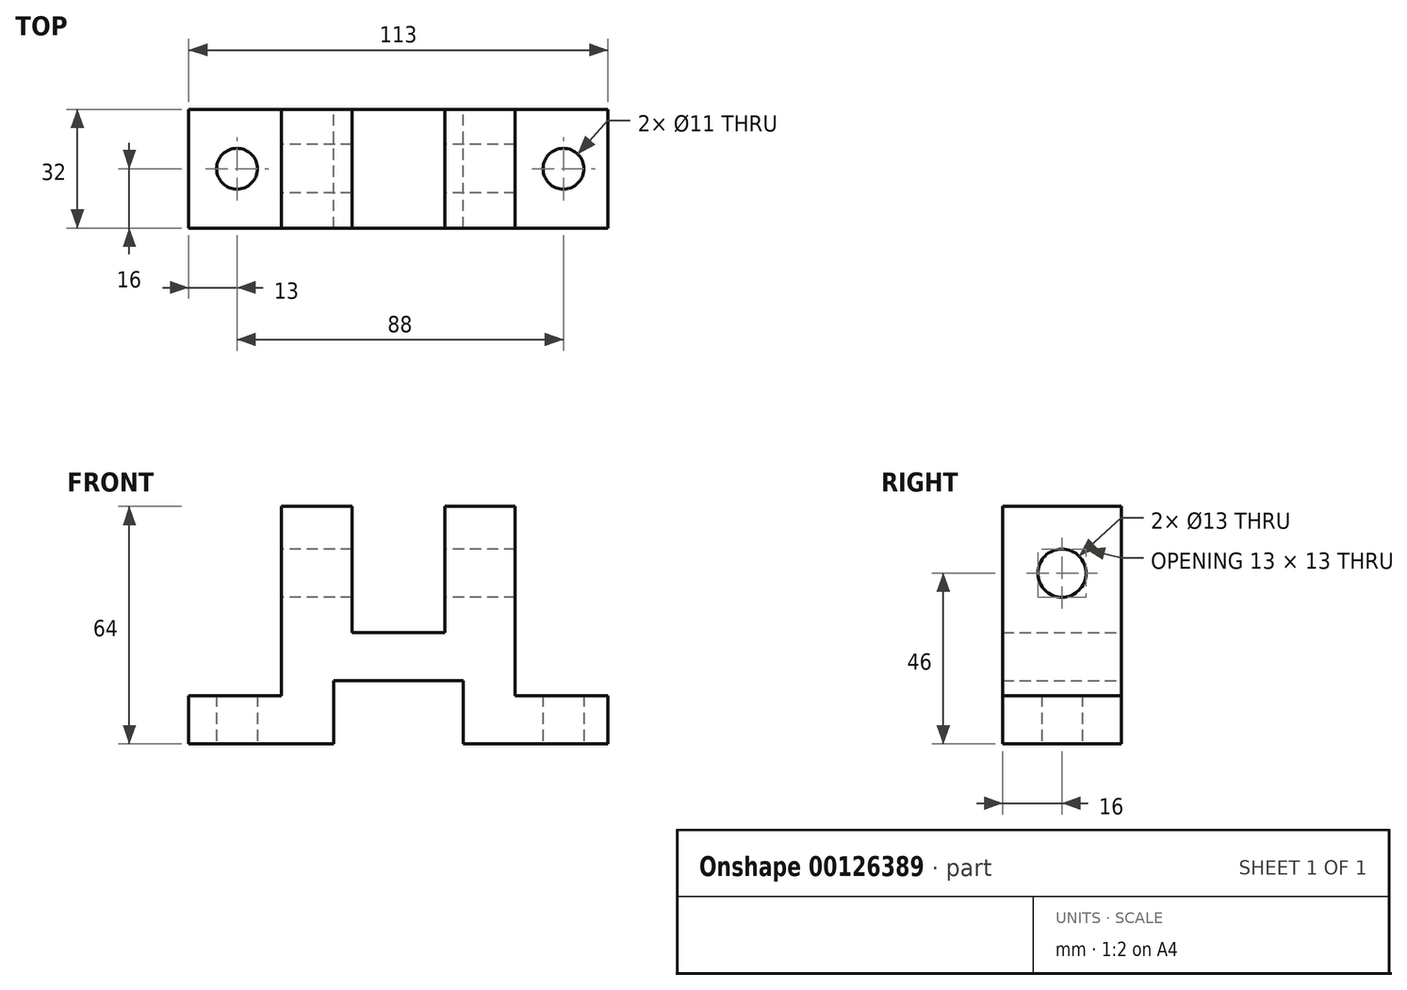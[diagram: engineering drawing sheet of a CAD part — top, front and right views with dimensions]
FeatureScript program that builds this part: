
annotation { "Feature Type Name" : "Feature", "Feature Type Description" : "" }
export const myFeature = defineFeature(function(context is Context, id is Id, definition is map)
    precondition{}
    {
        {
            var Q0;
            Q0=qCreatedBy(makeId("Front.planeOp"),FACE);
            var sketch = newSketch(context, id + "F0", { "sketchPlane" : qUnion([Q0])});
            skLineSegment(sketch, "E0", {"start": v(0, 0) * mm, "end": v(0, 13) * mm});
            skLineSegment(sketch, "E1", {"start": v(0, 13) * mm, "end": v(25, 13) * mm});
            skLineSegment(sketch, "E2", {"start": v(25, 13) * mm, "end": v(25, 64) * mm});
            skLineSegment(sketch, "E3", {"start": v(25, 64) * mm, "end": v(44, 64) * mm});
            skLineSegment(sketch, "E4", {"start": v(44, 64) * mm, "end": v(44, 30) * mm});
            skLineSegment(sketch, "E5", {"start": v(44, 30) * mm, "end": v(69, 30) * mm});
            skLineSegment(sketch, "E6", {"start": v(69, 30) * mm, "end": v(69, 64) * mm});
            skLineSegment(sketch, "E7", {"start": v(69, 64) * mm, "end": v(88, 64) * mm});
            skLineSegment(sketch, "E8", {"start": v(88, 64) * mm, "end": v(88, 13) * mm});
            skLineSegment(sketch, "E9", {"start": v(88, 13) * mm, "end": v(113, 13) * mm});
            skLineSegment(sketch, "E10", {"start": v(113, 13) * mm, "end": v(113, 0) * mm});
            skLineSegment(sketch, "E11", {"start": v(113, 0) * mm, "end": v(74, 0) * mm});
            skLineSegment(sketch, "E12", {"start": v(74, 0) * mm, "end": v(74, 17) * mm});
            skLineSegment(sketch, "E13", {"start": v(74, 17) * mm, "end": v(39, 17) * mm});
            skLineSegment(sketch, "E14", {"start": v(39, 17) * mm, "end": v(39, 0) * mm});
            skLineSegment(sketch, "E15", {"start": v(39, 0) * mm, "end": v(0, 0) * mm});
            skSolve(sketch);
        }
        {
            var Q0;
            Q0 = qSketchRegion(id + "F0", true);
            extrude(context, id + "F1", {"entities" : qUnion([Q0]), "depth" : 32 * mm});
        }
        {
            var Q0;
            Q0=qCreatedBy(makeId("Right.planeOp"),FACE);
            var sketch = newSketch(context, id + "F2", { "sketchPlane" : qUnion([Q0])});
            skCircle(sketch, "E16", {"center": v(-16, 46) * mm, "radius": 6.5 * mm});
            skLineSegment(sketch, "E17", {"start": v(-16, 64) * mm, "end": v(-16, 28) * mm, "construction": true});
            skSolve(sketch);
        }
        {
            var Q0;
            Q0=makeQuery(id+"F2.imprint","IMPRINT",FACE,{"disambiguationData":[TD([[makeQuery(id+"F2.imprint","IMPRINT",EDGE,{"derivedFrom":sQuery(id+"F2.wireOp",EDGE,"E16")}),1.0]])]});
            extrude(context, id + "F3", {"entities" : qUnion([Q0]), "operationType" : NewBodyOperationType.REMOVE, "endBound" : BoundingType.THROUGH_ALL, "depth" : 25 * mm});
        }
        {
            var Q0;
            Q0=qCreatedBy(makeId("Top.planeOp"),FACE);
            var sketch = newSketch(context, id + "F4", { "sketchPlane" : qUnion([Q0])});
            skLineSegment(sketch, "E18", {"start": v(13, 0) * mm, "end": v(13, -32) * mm, "construction": true});
            skCircle(sketch, "E19", {"center": v(13, -16) * mm, "radius": 5.5 * mm});
            skSolve(sketch);
        }
        {
            var Q0;
            Q0 = qSketchRegion(id + "F4", true);
            extrude(context, id + "F5", {"entities" : qUnion([Q0]), "operationType" : NewBodyOperationType.REMOVE, "depth" : 25 * mm});
        }
        {
            var Q0;
            Q0=qCreatedBy(makeId("Top.planeOp"),FACE);
            var sketch = newSketch(context, id + "F6", { "sketchPlane" : qUnion([Q0])});
            skCircle(sketch, "E20", {"center": v(101, -16) * mm, "radius": 5.5 * mm});
            skLineSegment(sketch, "E21", {"start": v(101, 0) * mm, "end": v(101, -39.94) * mm, "construction": true});
            skSolve(sketch);
        }
        {
            var Q0;
            Q0 = qSketchRegion(id + "F6", true);
            extrude(context, id + "F7", {"entities" : qUnion([Q0]), "operationType" : NewBodyOperationType.REMOVE, "depth" : 25 * mm});
        }
    });
